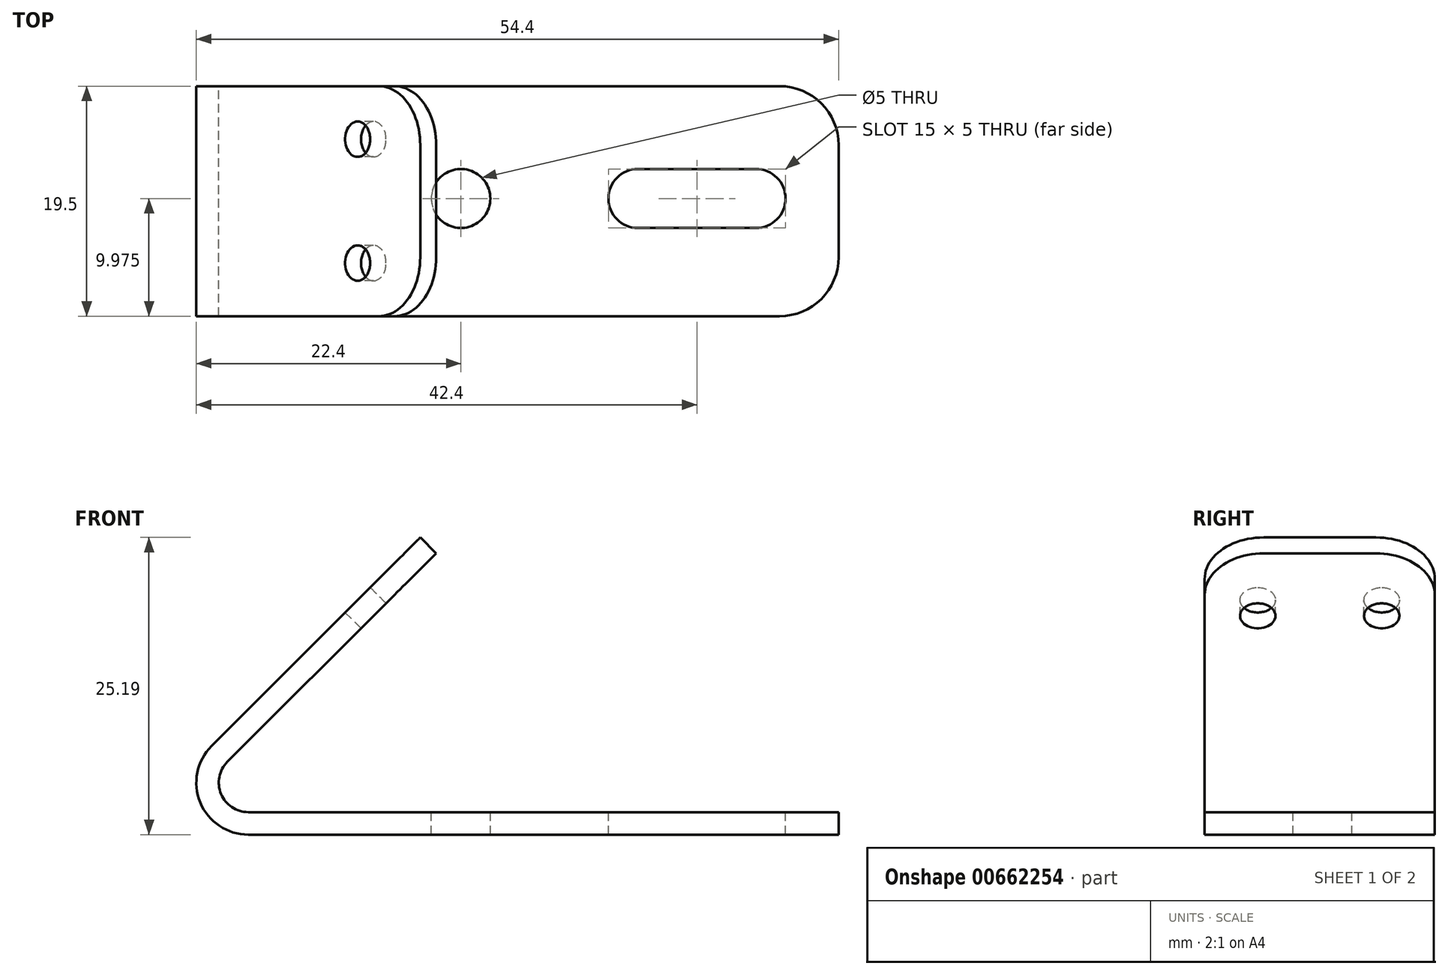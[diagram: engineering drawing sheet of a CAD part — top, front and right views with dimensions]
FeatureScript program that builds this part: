
annotation { "Feature Type Name" : "Feature", "Feature Type Description" : "" }
export const myFeature = defineFeature(function(context is Context, id is Id, definition is map)
    precondition{}
    {
        {
            var Q0;
            Q0=qCreatedBy(makeId("Front.planeOp"),FACE);
            var sketch = newSketch(context, id + "F0", { "sketchPlane" : qUnion([Q0])});
            skLineSegment(sketch, "E0", {"start": v(0, 0) * mm, "end": v(-50, 0) * mm});
            skLineSegment(sketch, "E1", {"start": v(-53.11, 7.51) * mm, "end": v(-35.43, 25.19) * mm});
            skArc(sketch, "E2", {"start": v(-53.11, 7.51) * mm, "mid": v(-54.07, 2.72) * mm, "end": v(-50, 0) * mm});
            skArc(sketch, "E3", {"start": v(-51.77, 6.17) * mm, "mid": v(-52.3, 3.44) * mm, "end": v(-50, 1.9) * mm});
            skLineSegment(sketch, "E4", {"start": v(-51.77, 6.17) * mm, "end": v(-34.1, 23.85) * mm});
            skLineSegment(sketch, "E5", {"start": v(-50, 1.9) * mm, "end": v(0, 1.9) * mm});
            skLineSegment(sketch, "E6", {"start": v(0, 1.9) * mm, "end": v(0, 0) * mm});
            skLineSegment(sketch, "E7", {"start": v(-35.43, 25.19) * mm, "end": v(-34.1, 23.85) * mm});
            skSolve(sketch);
        }
        {
            var Q0;
            Q0=makeQuery(id+"F0.imprint","IMPRINT",FACE,{"disambiguationData":[TD([[makeQuery(id+"F0.imprint","IMPRINT",EDGE,{"derivedFrom":sQuery(id+"F0.wireOp",EDGE,"E0")}),-1.0]])]});
            extrude(context, id + "F1", {"entities" : qUnion([Q0]), "depth" : 19.5 * mm, "offsetDistance" : 25 * mm});
        }
        {
            var Q0;
            Q0=makeQuery(id+"F1.opExtrude","SWEPT_FACE",FACE,{"disambiguationData":[OSD([sQuery(id+"F0.wireOp",EDGE,"E5")])]});
            var sketch = newSketch(context, id + "F2", { "sketchPlane" : qUnion([Q0])});
            skCircle(sketch, "E8", {"center": v(-17, -9.53) * mm, "radius": 2.5 * mm});
            skCircle(sketch, "E9", {"center": v(-7, -9.53) * mm, "radius": 2.5 * mm});
            skLineSegment(sketch, "E10", {"start": v(-17, -7.03) * mm, "end": v(-7, -7.02) * mm});
            skLineSegment(sketch, "E11", {"start": v(-17, -12.02) * mm, "end": v(-7, -12.02) * mm});
            skCircle(sketch, "E12", {"center": v(-32, -9.53) * mm, "radius": 2.5 * mm});
            skSolve(sketch);
        }
        {
            var Q0;
            {var subQ0=sQuery(id+"F2.wireOp",EDGE,"E8");var subQ1=makeQuery(id+"F2.imprint","INTERSECT",VERTEX,{"derivedFrom":[subQ0,sQuery(id+"F2.wireOp",EDGE,"E10")]});Q0=makeQuery(id+"F2.imprint","IMPRINT",FACE,{"disambiguationData":[TD([[makeQuery(id+"F2.imprint","IMPRINT",EDGE,{"disambiguationData":[TD([[subQ1,-1.0]])],"derivedFrom":subQ0}),1.0]])]});}
            var Q1;
            {var subQ0=sQuery(id+"F2.wireOp",EDGE,"E10");Q1=makeQuery(id+"F2.imprint","IMPRINT",FACE,{"disambiguationData":[TD([[makeQuery(id+"F2.imprint","IMPRINT",EDGE,{"derivedFrom":subQ0}),-1.0]])]});}
            var Q2;
            {var subQ0=sQuery(id+"F2.wireOp",EDGE,"E9");var subQ1=makeQuery(id+"F2.imprint","INTERSECT",VERTEX,{"derivedFrom":[subQ0,sQuery(id+"F2.wireOp",EDGE,"E10")]});Q2=makeQuery(id+"F2.imprint","IMPRINT",FACE,{"disambiguationData":[TD([[makeQuery(id+"F2.imprint","IMPRINT",EDGE,{"disambiguationData":[TD([[subQ1,-1.0]])],"derivedFrom":subQ0}),1.0]])]});}
            var Q3;
            Q3=makeQuery(id+"F2.imprint","IMPRINT",FACE,{"disambiguationData":[TD([[makeQuery(id+"F2.imprint","IMPRINT",EDGE,{"derivedFrom":sQuery(id+"F2.wireOp",EDGE,"E12")}),1.0]])]});
            extrude(context, id + "F3", {"entities" : qUnion([Q0, Q1, Q2, Q3]), "operationType" : NewBodyOperationType.REMOVE, "oppositeDirection" : true, "depth" : 25 * mm, "offsetDistance" : 25 * mm});
        }
        {
            var Q0;
            Q0=makeQuery(id+"F1.opExtrude","SWEPT_FACE",FACE,{"disambiguationData":[OSD([sQuery(id+"F0.wireOp",EDGE,"E1")])]});
            var sketch = newSketch(context, id + "F4", { "sketchPlane" : qUnion([Q0])});
            skCircle(sketch, "E13", {"center": v(4.5, -14.74) * mm, "radius": 1.5 * mm});
            skCircle(sketch, "E14", {"center": v(15, -14.74) * mm, "radius": 1.5 * mm});
            skSolve(sketch);
        }
        {
            var Q0;
            Q0=makeQuery(id+"F4.imprint","IMPRINT",FACE,{"disambiguationData":[TD([[makeQuery(id+"F4.imprint","IMPRINT",EDGE,{"derivedFrom":sQuery(id+"F4.wireOp",EDGE,"E13")}),1.0]])]});
            var Q1;
            Q1=makeQuery(id+"F4.imprint","IMPRINT",FACE,{"disambiguationData":[TD([[makeQuery(id+"F4.imprint","IMPRINT",EDGE,{"derivedFrom":sQuery(id+"F4.wireOp",EDGE,"E14")}),1.0]])]});
            extrude(context, id + "F5", {"entities" : qUnion([Q0, Q1]), "operationType" : NewBodyOperationType.REMOVE, "oppositeDirection" : true, "depth" : 12 * mm, "offsetDistance" : 25 * mm});
        }
        {
            var Q0;
            Q0=makeQuery(id+"F1.opExtrude","CAP_EDGE",EDGE,{"disambiguationData":[OSD([sQuery(id+"F0.wireOp",EDGE,"E7")])],"isStart":true});
            var Q1;
            Q1=makeQuery(id+"F1.opExtrude","CAP_EDGE",EDGE,{"disambiguationData":[OSD([sQuery(id+"F0.wireOp",EDGE,"E7")])],"isStart":false});
            var Q2;
            Q2=makeQuery(id+"F1.opExtrude","CAP_EDGE",EDGE,{"disambiguationData":[OSD([sQuery(id+"F0.wireOp",EDGE,"E6")])],"isStart":false});
            var Q3;
            Q3=makeQuery(id+"F1.opExtrude","CAP_EDGE",EDGE,{"disambiguationData":[OSD([sQuery(id+"F0.wireOp",EDGE,"E6")])],"isStart":true});
            fillet(context, id + "F6", {"entities" : qUnion([Q0, Q1, Q2, Q3]), "radius" : 5 * mm, "tangentPropagation" : true, "allowEdgeOverflow" : false});
        }
    });
